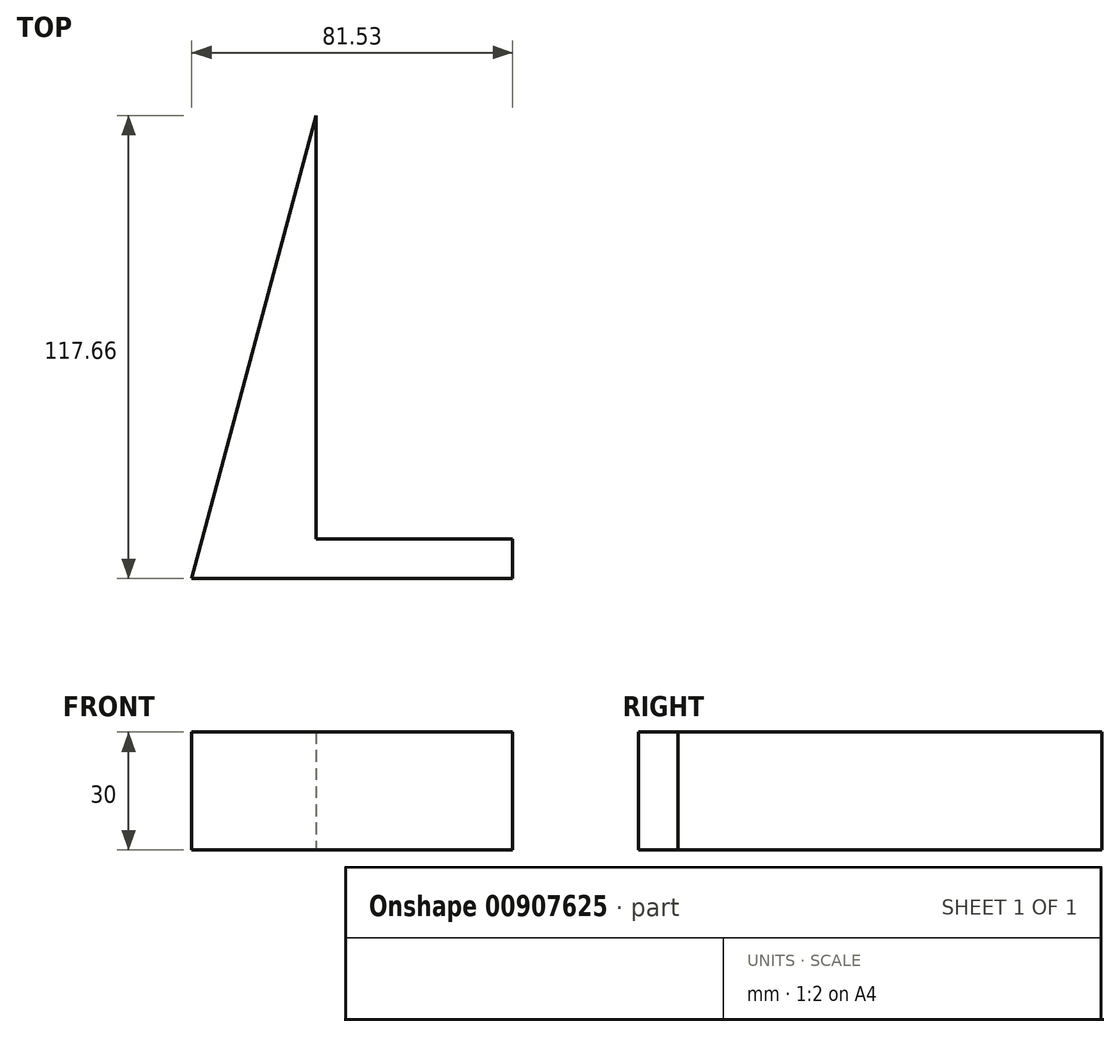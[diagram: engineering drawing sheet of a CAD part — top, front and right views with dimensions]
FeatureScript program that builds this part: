
annotation { "Feature Type Name" : "Feature", "Feature Type Description" : "" }
export const myFeature = defineFeature(function(context is Context, id is Id, definition is map)
    precondition{}
    {
        {
            var Q0;
            Q0=qCreatedBy(makeId("Top.planeOp"),FACE);
            var sketch = newSketch(context, id + "F0", { "sketchPlane" : qUnion([Q0])});
            skLineSegment(sketch, "E0", {"start": v(0, 0) * mm, "end": v(-81.53, 0) * mm});
            skLineSegment(sketch, "E1", {"start": v(-81.53, 0) * mm, "end": v(-50, 117.66) * mm});
            skLineSegment(sketch, "E2", {"start": v(-81.53, 0) * mm, "end": v(0, 304.27) * mm, "construction": true});
            skLineSegment(sketch, "E3", {"start": v(0, 0) * mm, "end": v(0, 304.27) * mm, "construction": true});
            skLineSegment(sketch, "E4", {"start": v(-50, 117.66) * mm, "end": v(-50, 10) * mm});
            skLineSegment(sketch, "E5", {"start": v(-50, 10) * mm, "end": v(0, 10) * mm});
            skLineSegment(sketch, "E6", {"start": v(0, 10) * mm, "end": v(0, 0) * mm});
            skSolve(sketch);
        }
        {
            var Q0;
            Q0 = qSketchRegion(id + "F0", true);
            extrude(context, id + "F1", {"entities" : qUnion([Q0]), "depth" : 30 * mm, "offsetDistance" : 25 * mm});
        }
    });
